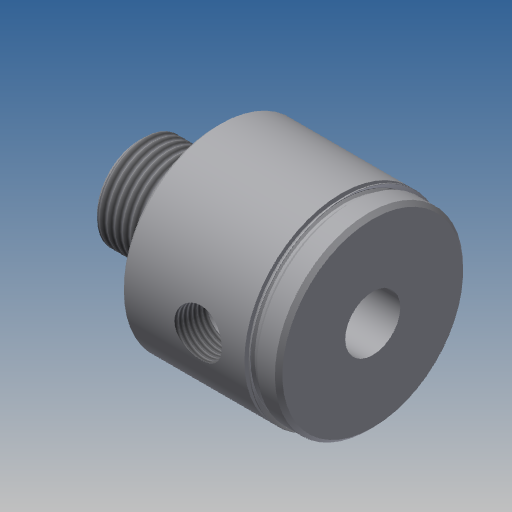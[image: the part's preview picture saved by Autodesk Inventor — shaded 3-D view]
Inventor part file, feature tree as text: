
AUTODESK INVENTOR PART (.ipt)
format: ipt  version: 2020 (Build 240168000, 168)  size: 301,056 bytes
history: native  units: in
note: dims shown in document units (in); Inventor stores cm internally (conversion verified against a paired STEP export)
features: other x119, sketch x5, revolve x4, thread x2, hole x1
ambient origin geometry x8: Origin, YZ Plane, XZ Plane, XY Plane, X Axis, Y Axis, Z Axis, Center Point
bodies: Solid1 (feature_tree)
feature tree (131):
  revolve  "Revolution1"  [1 undecoded]
  thread  "Thread1"  [1 undecoded]
  revolve  "Revolution2"  Angle=360.0deg
  hole  "Hole1"  [1 undecoded]
  revolve  "Revolution3"  [1 undecoded]
  thread  "Thread2"  [1 undecoded]
  revolve  "Revolution4"  [1 undecoded]
  other  "dp1_XY"
  other  "dp1_YZ"
  other  "dp1_ZX"
  other  "dp1_X"
  other  "dp1_Y"
  other  "dp1_Z"
  other  "dp1_Center"
  other  "dp2_XY"
  other  "dp2_YZ"
  other  "dp2_ZX"
  other  "dp2_X"
  other  "dp2_Y"
  other  "dp2_Z"
  other  "dp2_Center"
  other  "hh_XY"
  other  "hh_YZ"
  other  "hh_ZX"
  other  "hh_X"
  other  "hh_Y"
  other  "hh_Z"
  other  "hh_Center"
  other  "port_XY"
  other  "port_YZ"
  other  "port_ZX"
  other  "port_X"
  other  "port_Y"
  other  "port_Z"
  other  "port_Center"
  other  "rod_guide_XY"
  other  "rod_guide_YZ"
  other  "rod_guide_ZX"
  other  "rod_guide_X"
  other  "rod_guide_Y"
  other  "rod_guide_Z"
  other  "rod_guide_Center"
  other  "s1_XY"
  other  "s1_YZ"
  other  "s1_ZX"
  other  "s1_X"
  other  "s1_Y"
  other  "s1_Z"
  other  "s1_Center"
  other  "s2_XY"
  other  "s2_YZ"
  other  "s2_ZX"
  other  "s2_X"
  other  "s2_Y"
  other  "s2_Z"
  other  "s2_Center"
  other  "t1_XY"
  other  "t1_YZ"
  other  "t1_ZX"
  other  "t1_X"
  other  "t1_Y"
  other  "t1_Z"
  other  "t1_Center"
  other  "t111_XY"
  other  "t111_YZ"
  other  "t111_ZX"
  other  "t111_X"
  other  "t111_Y"
  other  "t111_Z"
  other  "t111_Center"
  other  "to_foot_bracket_XY"
  other  "to_foot_bracket_YZ"
  other  "to_foot_bracket_ZX"
  other  "to_foot_bracket_X"
  other  "to_foot_bracket_Y"
  other  "to_foot_bracket_Z"
  other  "to_foot_bracket_Center"
  other  "to_nut_XY"
  other  "to_nut_YZ"
  other  "to_nut_ZX"
  other  "to_nut_X"
  other  "to_nut_Y"
  other  "to_nut_Z"
  other  "to_nut_Center"
  other  "to_rod_XY"
  other  "to_rod_YZ"
  other  "to_rod_ZX"
  other  "to_rod_X"
  other  "to_rod_Y"
  other  "to_rod_Z"
  other  "to_rod_Center"
  other  "to_screw_XY"
  other  "to_screw_YZ"
  other  "to_screw_ZX"
  other  "to_screw_X"
  other  "to_screw_Y"
  other  "to_screw_Z"
  other  "to_screw_Center"
  other  "to_trunnion_brackets_XY"
  other  "to_trunnion_brackets_YZ"
  other  "to_trunnion_brackets_ZX"
  other  "to_trunnion_brackets_X"
  other  "to_trunnion_brackets_Y"
  other  "to_trunnion_brackets_Z"
  other  "to_trunnion_brackets_Center"
  other  "to_trunnion_brackets1_XY"
  other  "to_trunnion_brackets1_YZ"
  other  "to_trunnion_brackets1_ZX"
  other  "to_trunnion_brackets1_X"
  other  "to_trunnion_brackets1_Y"
  other  "to_trunnion_brackets1_Z"
  other  "to_trunnion_brackets1_Center"
  other  "to_trunnion_brackets2_XY"
  other  "to_trunnion_brackets2_YZ"
  other  "to_trunnion_brackets2_ZX"
  other  "to_trunnion_brackets2_X"
  other  "to_trunnion_brackets2_Y"
  other  "to_trunnion_brackets2_Z"
  other  "to_trunnion_brackets2_Center"
  other  "to_tube_XY"
  other  "to_tube_YZ"
  other  "to_tube_ZX"
  other  "to_tube_X"
  other  "to_tube_Y"
  other  "to_tube_Z"
  other  "to_tube_Center"
  sketch  "Sketch_2"  dims[d0=360.0deg d1=0.3297in d2=0.0in d3=360.0deg]
  sketch  "Sketch_3"  dims[d4=0.442in d5=0.75in d6=0.502in d7=0.25in d8=90.0deg d9=1.875in d10=0.0in d11=360.0deg]
  sketch  "Sketch3"  dims[d12=0.2521in d13=0.0in d14=360.0deg]
  sketch  "Sketch_40"  dims[d15=0.0in d16=0.0in d17=0.0in d18=0.0in d19=0.0in d20=0.0in]
  sketch  "Sketch_47"
note: 6 required parameter values undecoded (feature->parameter linkage not recoverable at this tier; creation-order binding heuristic only, values carry confidence <= 0.55)